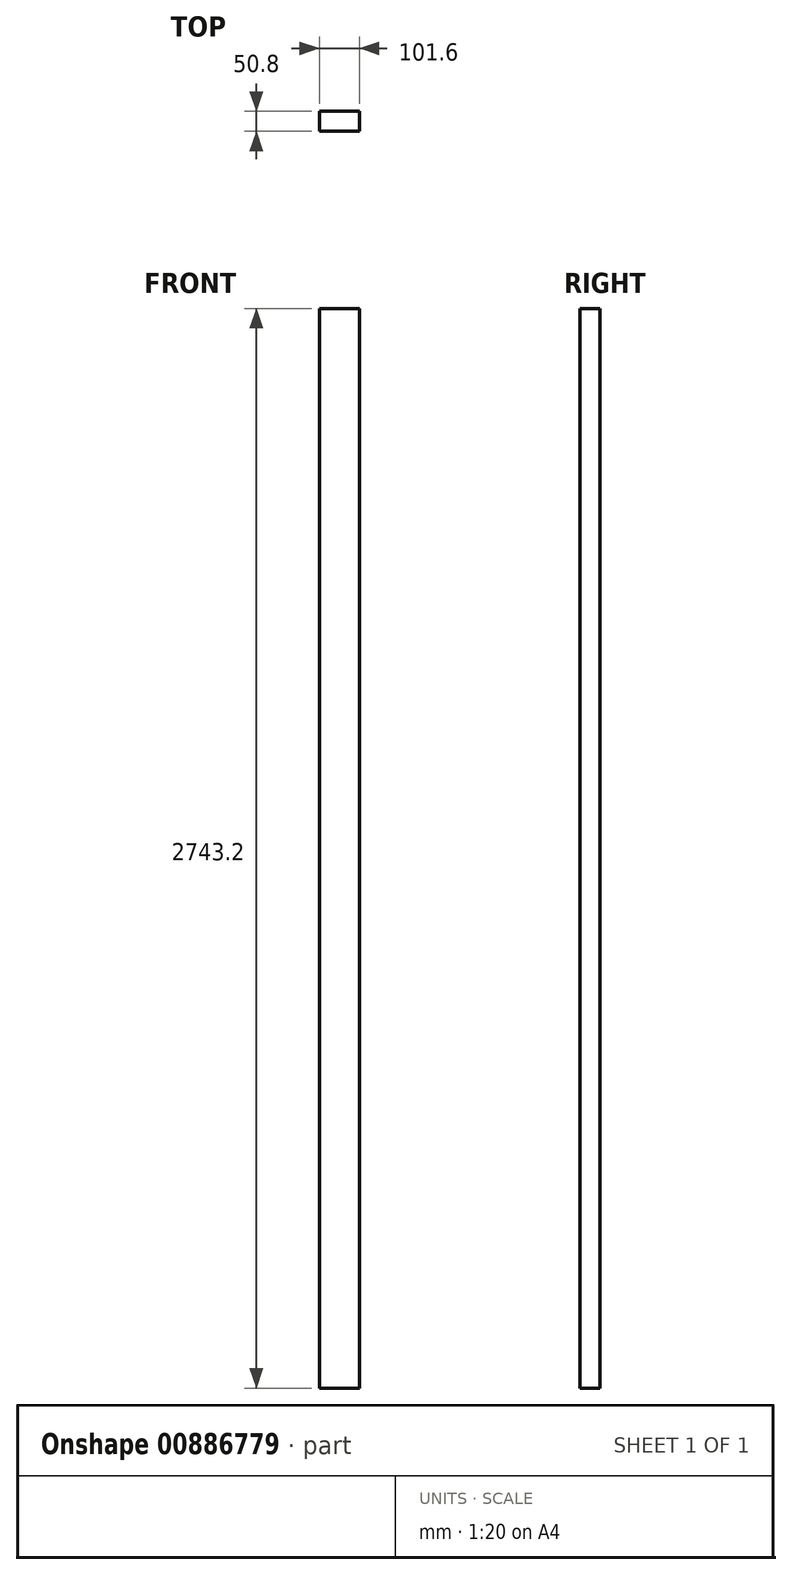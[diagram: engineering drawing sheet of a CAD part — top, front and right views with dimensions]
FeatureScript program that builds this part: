
annotation { "Feature Type Name" : "Feature", "Feature Type Description" : "" }
export const myFeature = defineFeature(function(context is Context, id is Id, definition is map)
    precondition{}
    {
        {
            var Q0;
            Q0=qCreatedBy(makeId("Front.planeOp"),FACE);
            var sketch = newSketch(context, id + "F0", { "sketchPlane" : qUnion([Q0])});
            skLineSegment(sketch, "E0.bottom", {"start": v(-50.8, 1371.6) * mm, "end": v(50.8, 1371.6) * mm});
            skLineSegment(sketch, "E0.top", {"start": v(-50.8, -1371.6) * mm, "end": v(50.8, -1371.6) * mm});
            skLineSegment(sketch, "E0.left", {"start": v(-50.8, 1371.6) * mm, "end": v(-50.8, -1371.6) * mm});
            skLineSegment(sketch, "E0.right", {"start": v(50.8, 1371.6) * mm, "end": v(50.8, -1371.6) * mm});
            skPoint(sketch, "E0.middle", {"position": v(0, 0) * mm});
            skSolve(sketch);
        }
        {
            var Q0;
            Q0=makeQuery(id+"F0.imprint","IMPRINT",FACE,{"disambiguationData":[TD([[makeQuery(id+"F0.imprint","IMPRINT",EDGE,{"derivedFrom":sQuery(id+"F0.wireOp",EDGE,"E0.bottom")}),-1.0]])]});
            extrude(context, id + "F1", {"entities" : qUnion([Q0]), "depth" : 50.8 * mm, "offsetDistance" : 25.4 * mm});
        }
    });
